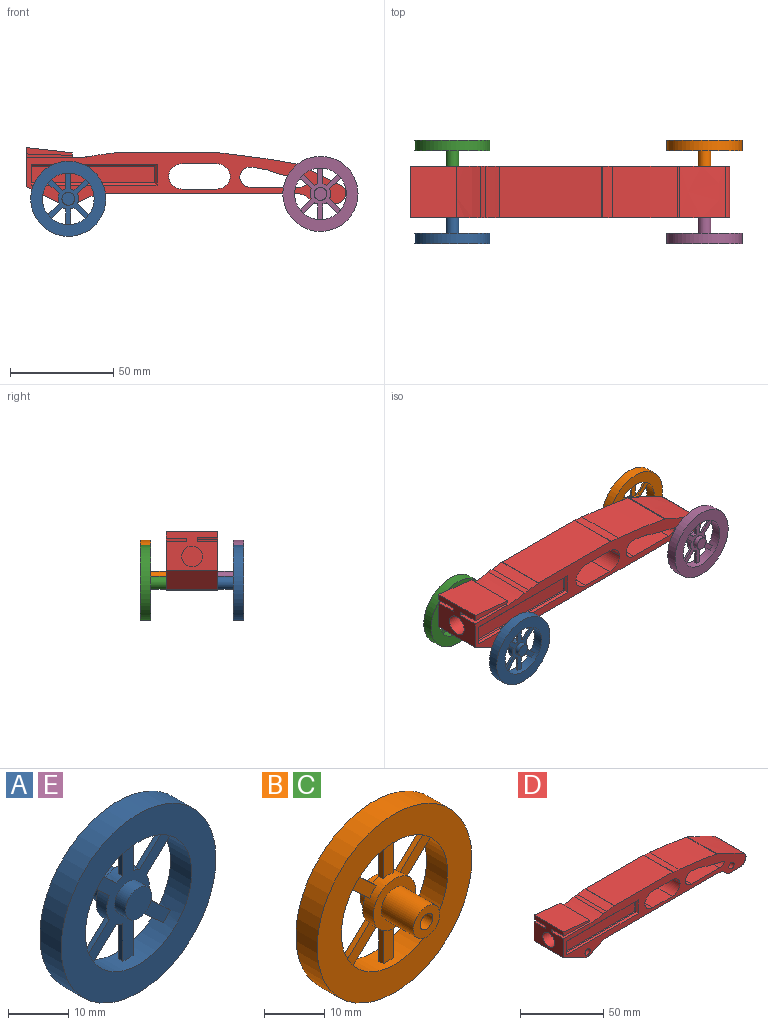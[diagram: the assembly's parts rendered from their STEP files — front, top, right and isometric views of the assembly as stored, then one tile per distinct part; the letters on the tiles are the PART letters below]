
ASSEMBLY  parts=5 mates=4
PART A: 31 faces, bbox 36.4x12.5x36.4 mm
  f0: cylinder r=3.1mm len=7.5mm, axis (0,1,0), area 146.1mm2, adj f2,f5
  f1: cylinder r=1.5mm len=10mm, axis (0,1,0), area 94.2mm2, adj f2,f3
  f2: plane 6.2x6.2mm, normal (0,1,0), area 23.1mm2, adj f0,f1
  f3: plane 3x3mm, normal (0,1,0), area 7.1mm2, adj f1
  f4: cylinder r=5mm len=10mm, axis (0,-1,0), area 64mm2, adj f5,f6,f9,f10,f11,f12,f13,f14
  f5: plane 10x10mm, normal (0,1,0), area 48.3mm2, adj f0,f4
  f6: plane 25.02x19.87mm, normal (0,-1,0), area 156.8mm2, adj f4,f8,f9,f10,f12,f13,f15,f16
  f7: plane 6.18x6.18mm, normal (0,-1,0), area 30mm2, adj f8
  f8: cylinder r=3.09mm len=6.18mm, axis (0,1,0), area 48.5mm2, adj f6,f7
  f9: plane 5.55x5.17mm, normal (0.68,0,-0.73), area 7.6mm2, adj f4,f6,f11,f27
  f10: plane 5.55x5.17mm, normal (-0.68,0,0.73), area 7.6mm2, adj f4,f6,f11,f27
  f11: plane 7.19x6.93mm, normal (0,1,0), area 18.1mm2, adj f4,f9,f10,f27
  f12: plane 7.59x1mm, normal (1,0,0), area 7.6mm2, adj f4,f6,f14,f27
  f13: plane 7.59x1mm, normal (-1,0,0), area 7.6mm2, adj f4,f6,f14,f27
  f14: plane 7.65x2.4mm, normal (0,1,0), area 18.1mm2, adj f4,f12,f13,f27
  f15: plane 5.55x5.17mm, normal (-0.68,0,-0.73), area 7.6mm2, adj f4,f6,f17,f27
  f16: plane 5.55x5.17mm, normal (0.68,0,0.73), area 7.6mm2, adj f4,f6,f17,f27
  f17: plane 7.19x6.93mm, normal (0,1,0), area 18.1mm2, adj f4,f15,f16,f27
  f18: plane 5.55x5.17mm, normal (-0.68,0,0.73), area 7.6mm2, adj f4,f6,f20,f27
  f19: plane 5.55x5.17mm, normal (0.68,0,-0.73), area 7.6mm2, adj f4,f6,f20,f27
  f20: plane 7.19x6.93mm, normal (0,1,0), area 18.1mm2, adj f4,f18,f19,f27
  f21: plane 7.59x1mm, normal (-1,0,0), area 7.6mm2, adj f4,f6,f23,f27
  f22: plane 7.59x1mm, normal (1,0,0), area 7.6mm2, adj f4,f6,f23,f27
  f23: plane 7.65x2.4mm, normal (0,1,0), area 18.1mm2, adj f4,f21,f22,f27
  f24: plane 5.55x5.17mm, normal (-0.68,0,-0.73), area 7.6mm2, adj f4,f6,f26,f27
  f25: plane 5.55x5.17mm, normal (0.68,0,0.73), area 7.6mm2, adj f4,f6,f26,f27
  f26: plane 7.19x6.93mm, normal (0,1,0), area 18.1mm2, adj f4,f24,f25,f27
  f27: cylinder r=12.5mm len=25mm, axis (0,1,0), area 378.3mm2, adj f6,f9,f10,f11,f12,f13,f14,f15
  f28: cylinder r=18.2mm len=36.4mm, axis (0,1,0), area 571.8mm2, adj f29,f30
  f29: plane 36.4x36.4mm, normal (0,-1,0), area 549.7mm2, adj f27,f28
  f30: plane 36.4x36.4mm, normal (0,1,0), area 549.7mm2, adj f27,f28
PART B: 31 faces, bbox 36.4x12.5x36.4 mm
  f0: cylinder r=3.1mm len=7.5mm, axis (0,-1,0), area 146.1mm2, adj f2,f5
  f1: cylinder r=1.5mm len=10mm, axis (0,-1,0), area 94.2mm2, adj f2,f3
  f2: plane 6.2x6.2mm, normal (0,-1,0), area 23.1mm2, adj f0,f1
  f3: plane 3x3mm, normal (0,-1,0), area 7.1mm2, adj f1
  f4: cylinder r=5mm len=10mm, axis (0,1,0), area 64mm2, adj f5,f6,f9,f10,f11,f12,f13,f14
  f5: plane 10x10mm, normal (0,-1,0), area 48.3mm2, adj f0,f4
  f6: plane 25.02x19.87mm, normal (0,1,0), area 156.8mm2, adj f4,f8,f9,f10,f12,f13,f15,f16
  f7: plane 6.18x6.18mm, normal (0,1,0), area 30mm2, adj f8
  f8: cylinder r=3.09mm len=6.18mm, axis (0,-1,0), area 48.5mm2, adj f6,f7
  f9: plane 5.55x5.17mm, normal (0.68,0,-0.73), area 7.6mm2, adj f4,f6,f11,f27
  f10: plane 5.55x5.17mm, normal (-0.68,0,0.73), area 7.6mm2, adj f4,f6,f11,f27
  f11: plane 7.19x6.93mm, normal (0,-1,0), area 18.1mm2, adj f4,f9,f10,f27
  f12: plane 7.59x1mm, normal (1,0,0), area 7.6mm2, adj f4,f6,f14,f27
  f13: plane 7.59x1mm, normal (-1,0,0), area 7.6mm2, adj f4,f6,f14,f27
  f14: plane 7.65x2.4mm, normal (0,-1,0), area 18.1mm2, adj f4,f12,f13,f27
  f15: plane 5.55x5.17mm, normal (-0.68,0,-0.73), area 7.6mm2, adj f4,f6,f17,f27
  f16: plane 5.55x5.17mm, normal (0.68,0,0.73), area 7.6mm2, adj f4,f6,f17,f27
  f17: plane 7.19x6.93mm, normal (0,-1,0), area 18.1mm2, adj f4,f15,f16,f27
  f18: plane 5.55x5.17mm, normal (-0.68,0,0.73), area 7.6mm2, adj f4,f6,f20,f27
  f19: plane 5.55x5.17mm, normal (0.68,0,-0.73), area 7.6mm2, adj f4,f6,f20,f27
  f20: plane 7.19x6.93mm, normal (0,-1,0), area 18.1mm2, adj f4,f18,f19,f27
  f21: plane 7.59x1mm, normal (-1,0,0), area 7.6mm2, adj f4,f6,f23,f27
  f22: plane 7.59x1mm, normal (1,0,0), area 7.6mm2, adj f4,f6,f23,f27
  f23: plane 7.65x2.4mm, normal (0,-1,0), area 18.1mm2, adj f4,f21,f22,f27
  f24: plane 5.55x5.17mm, normal (-0.68,0,-0.73), area 7.6mm2, adj f4,f6,f26,f27
  f25: plane 5.55x5.17mm, normal (0.68,0,0.73), area 7.6mm2, adj f4,f6,f26,f27
  f26: plane 7.19x6.93mm, normal (0,-1,0), area 18.1mm2, adj f4,f24,f25,f27
  f27: cylinder r=12.5mm len=25mm, axis (0,-1,0), area 378.3mm2, adj f6,f9,f10,f11,f12,f13,f14,f15
  f28: cylinder r=18.2mm len=36.4mm, axis (0,-1,0), area 571.8mm2, adj f29,f30
  f29: plane 36.4x36.4mm, normal (0,1,0), area 549.7mm2, adj f27,f28
  f30: plane 36.4x36.4mm, normal (0,-1,0), area 549.7mm2, adj f27,f28
PART C: same geometry as B
PART D: 64 faces, bbox 155x25x28.5 mm
  f0: plane 25x2.5mm, normal (1,0,0), area 32.2mm2, adj f1,f4,f50,f57,f58,f60,f61,f63
  f1: plane 22.46x3.22mm, normal (0,1,0), area 44.3mm2, adj f0,f3,f57,f61
  f2: plane 155.01x26mm, normal (0,1,0), area 1596.3mm2, adj f3,f6,f7,f8,f9,f10,f11,f12
  f3: plane 25x19.07mm, normal (-1,0,0), area 361mm2, adj f1,f2,f4,f5,f33,f37,f57,f58
  f4: plane 22.46x3.75mm, normal (0,-1,0), area 48.4mm2, adj f0,f3,f57,f58
  f5: plane 155.01x26mm, normal (0,-1,0), area 1596.3mm2, adj f3,f6,f7,f8,f9,f10,f11,f12
  f6: plane 25x8.1mm, normal (0,0,-1), area 202.4mm2, adj f2,f5,f24,f25
  f7: cylinder r=5mm len=25mm, axis (0,-1,0), area 34.3mm2, adj f2,f5,f22,f31
  f8: extruded ~31.63x25mm, area 799.5mm2, adj f2,f5,f11,f29
  f9: cylinder r=5mm len=25mm, axis (0,1,0), area 9mm2, adj f2,f5,f25,f27
  f10: cylinder r=5mm len=25mm, axis (0,-1,0), area 217.9mm2, adj f2,f5,f13,f22
  f11: cylinder r=12091.62mm len=25mm, axis (0,1,0), area 125.3mm2, adj f2,f5,f8,f18
  f12: cylinder r=5mm len=25mm, axis (0,-1,0), area 139.6mm2, adj f2,f5,f28,f30
  f13: cylinder r=5mm len=25mm, axis (0,-1,0), area 190mm2, adj f2,f5,f10,f28
  f14: cylinder r=6.76mm len=25mm, axis (0,1,0), area 249.4mm2, adj f2,f5,f15,f36
  f15: cylinder r=6.76mm len=25mm, axis (0,-1,0), area 249.4mm2, adj f2,f5,f14,f35
  f16: cylinder r=6.76mm len=25mm, axis (0,1,0), area 249.4mm2, adj f2,f5,f17,f35
  f17: cylinder r=6.76mm len=25mm, axis (0,-1,0), area 249.4mm2, adj f2,f5,f16,f36
  f18: cylinder r=1mm len=25mm, axis (0,-1,0), area 2.8mm2, adj f2,f5,f11,f21
  f19: cylinder r=2.25mm len=25mm, axis (0,-1,0), area 353.4mm2, adj f2,f5
  f20: plane 96.55x25mm, normal (0,0,-1), area 2413.8mm2, adj f2,f5,f34,f40
  f21: plane 49.44x25mm, normal (0,0,1), area 1236.1mm2, adj f2,f5,f18,f23
  f22: plane 25x7.26mm, normal (-0.17,0,-0.99), area 184.3mm2, adj f2,f5,f7,f10
  f23: extruded ~25x0.24mm, area 6.1mm2, adj f2,f5,f21,f49
  f24: cylinder r=5mm len=25mm, axis (0,-1,0), area 109.4mm2, adj f2,f5,f6,f40
  f25: cylinder r=5mm len=25mm, axis (0,1,0), area 131.5mm2, adj f2,f5,f6,f9
  f26: extruded ~25x22.42mm, area 620.5mm2, adj f2,f5,f27,f29
  f27: cylinder r=4.15mm len=25mm, axis (0,-1,0), area 169.3mm2, adj f2,f5,f9,f26
  f28: plane 25x24.01mm, normal (0,0,1), area 600.3mm2, adj f2,f5,f12,f13
  f29: cylinder r=5mm len=25mm, axis (0,1,0), area 20.4mm2, adj f2,f5,f8,f26
  f30: plane 25x15.06mm, normal (-0.24,0,-0.97), area 388mm2, adj f2,f5,f12,f31
  f31: plane 25x4.01mm, normal (-0.34,0,-0.94), area 106.6mm2, adj f2,f5,f7,f30
  f32: cylinder r=2.25mm len=25mm, axis (0,1,0), area 353.4mm2, adj f2,f5
  f33: plane 25x18.31mm, normal (-0.44,0,-0.9), area 509.1mm2, adj f2,f3,f5,f39
  f34: plane 25x11.74mm, normal (0.44,0,-0.9), area 326.6mm2, adj f2,f5,f20,f39
  f35: plane 25x16.58mm, normal (0,0,1), area 414.5mm2, adj f2,f5,f15,f16
  f36: plane 25x16.58mm, normal (0,0,-1), area 414.5mm2, adj f2,f5,f14,f17
  f37: cylinder r=5mm len=60mm, axis (-1,0,0), area 1885mm2, adj f3,f38
  f38: plane 10x10mm, normal (-1,0,0), area 78.5mm2, adj f37
  f39: cylinder r=5mm len=25mm, axis (0,1,0), area 113.3mm2, adj f2,f5,f33,f34
  f40: cylinder r=8.93mm len=25mm, axis (0,-1,0), area 195.4mm2, adj f2,f5,f20,f24
  f41: plane 10x2mm, normal (1,0,0), area 17mm2, adj f5,f42,f44,f45,f51,f52
  f42: plane 60x1mm, normal (0,0,1), area 60mm2, adj f41,f43,f45,f51
  f43: plane 8x1mm, normal (-1,0,0), area 8mm2, adj f42,f44,f45,f56
  f44: plane 60x1mm, normal (0,0,-1), area 60mm2, adj f41,f43,f45,f52
  f45: plane 60x8mm, normal (0,-1,0), area 480mm2, adj f41,f42,f43,f44
  f46: plane 10x1mm, normal (1,0,0), area 9mm2, adj f2,f47,f53,f54
  f47: plane 60x8mm, normal (0,1,0), area 480mm2, adj f46,f53,f54,f55
  f48: cylinder r=20mm len=25mm, axis (0,1,0), area 67mm2, adj f2,f5,f49,f50
  f49: cylinder r=160mm len=25mm, axis (0,-1,0), area 167.2mm2, adj f2,f5,f23,f48
  f50: cylinder r=51.86mm len=25mm, axis (0,1,0), area 292.4mm2, adj f0,f2,f5,f48,f59,f62
  f51: plane 61x1mm, normal (0,-0.71,0.71), area 85.6mm2, adj f5,f41,f42,f56
  f52: plane 61x1mm, normal (0,-0.71,-0.71), area 85.6mm2, adj f5,f41,f44,f56
  f53: plane 61x1mm, normal (0,0.71,-0.71), area 85.6mm2, adj f2,f46,f47,f55
  f54: plane 61x1mm, normal (0,0.71,0.71), area 85.6mm2, adj f2,f46,f47,f55
  f55: plane 10x1mm, normal (-0.71,0.71,0), area 12.7mm2, adj f2,f47,f53,f54
  f56: plane 10x1mm, normal (-0.71,-0.71,0), area 12.7mm2, adj f5,f43,f51,f52
  f57: plane 25x22.46mm, normal (0.11,0,0.99), area 564.9mm2, adj f0,f1,f3,f4
  f58: plane 22.46x10mm, normal (-0.03,0,-1), area 224.7mm2, adj f0,f3,f4,f60
  f59: plane 22.46x10mm, normal (0,0,1), area 224.6mm2, adj f3,f5,f50,f60
  f60: plane 22.46x1.94mm, normal (0,-1,0), area 35.9mm2, adj f0,f3,f58,f59
  f61: plane 22.46x10mm, normal (0,0,-1), area 224.6mm2, adj f0,f1,f3,f63
  f62: plane 22.46x10mm, normal (0,0,1), area 224.6mm2, adj f2,f3,f50,f63
  f63: plane 22.46x1.78mm, normal (0,1,0), area 40mm2, adj f0,f3,f61,f62
PART E: same geometry as A
PLACE A t=(-99.57,-5,-2.56)mm
PLACE B t=(22.61,-5,-0.16)mm
PLACE C t=(-99.57,-5,-2.56)mm
PLACE D t=(-0.87,20,32.3)mm
PLACE E t=(22.61,-5,-0.16)mm
MATE revolute B.f0 <-> D.f19  axis (0,-1,0) through (22.61,20,-0.16)mm
MATE revolute E.f0 <-> D.f19  axis (0,1,0) through (22.61,-5,-0.16)mm
MATE revolute C.f0 <-> D.f32  axis (0,-1,0) through (-99.57,20,-2.56)mm
MATE revolute A.f0 <-> D.f32  axis (0,1,0) through (-99.57,-5,-2.56)mm
